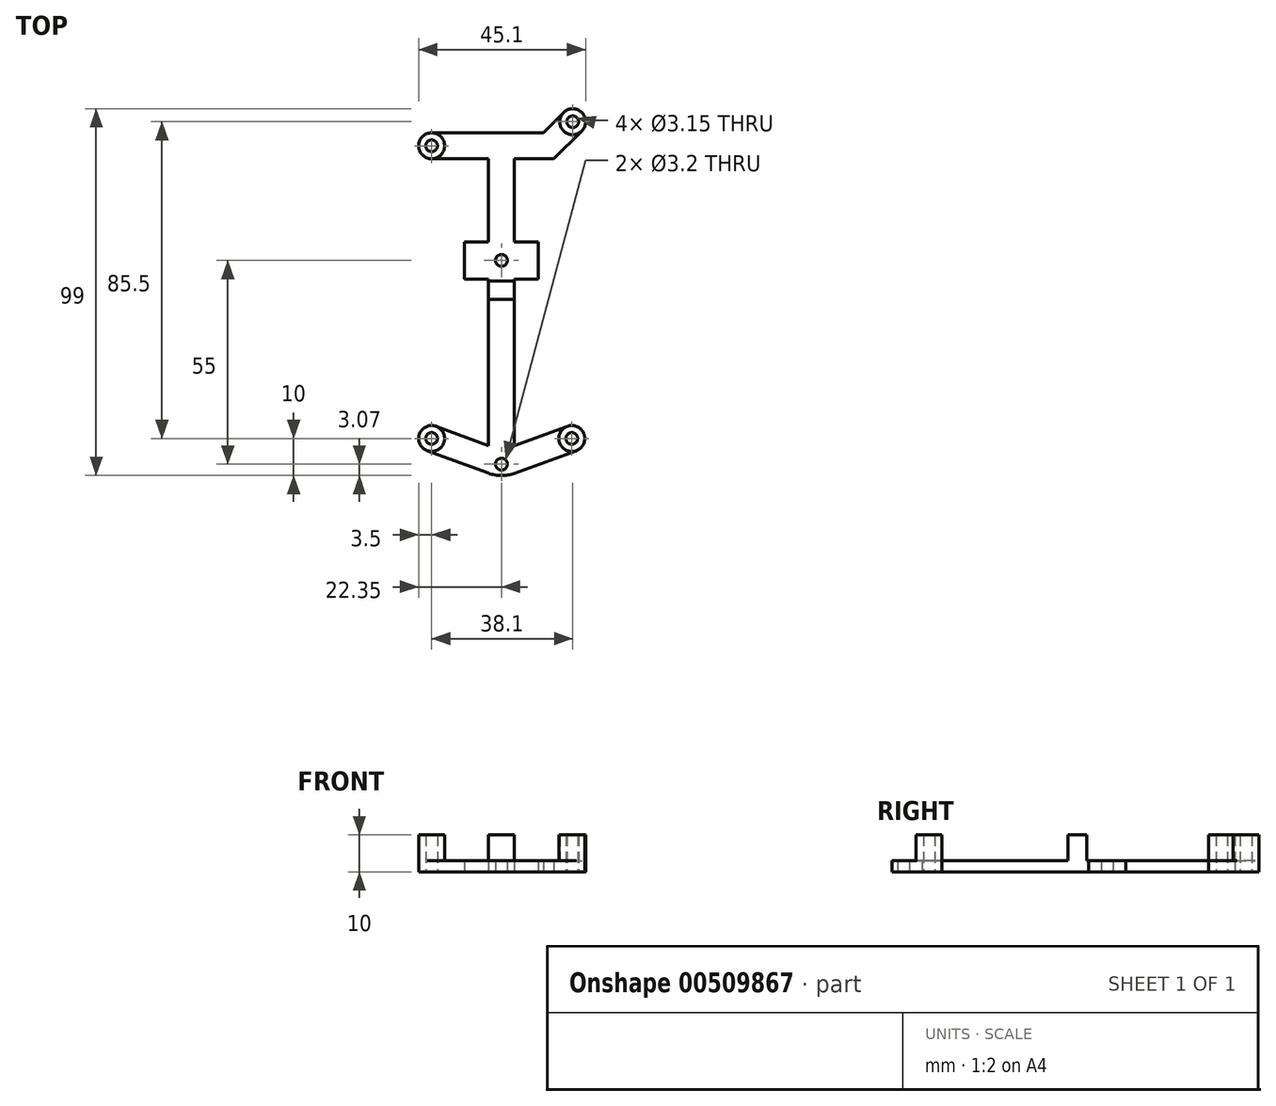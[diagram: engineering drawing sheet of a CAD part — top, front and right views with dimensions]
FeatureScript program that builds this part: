
annotation { "Feature Type Name" : "Feature", "Feature Type Description" : "" }
export const myFeature = defineFeature(function(context is Context, id is Id, definition is map)
    precondition{}
    {
        {
            var Q0;
            Q0=qCreatedBy(makeId("Top.planeOp"),FACE);
            var sketch = newSketch(context, id + "F0", { "sketchPlane" : qUnion([Q0])});
            skCircle(sketch, "E0", {"center": v(6.15, 89) * mm, "radius": 1.6 * mm, "construction": true});
            skCircle(sketch, "E1", {"center": v(44.25, 95.5) * mm, "radius": 1.6 * mm, "construction": true});
            skCircle(sketch, "E2", {"center": v(4.15, 55) * mm, "radius": 1.6 * mm, "construction": true});
            skCircle(sketch, "E3", {"center": v(6.15, 43) * mm, "radius": 1.6 * mm, "construction": true});
            skCircle(sketch, "E4", {"center": v(45.5, 43) * mm, "radius": 1.6 * mm, "construction": true});
            skCircle(sketch, "E5", {"center": v(6.15, 10) * mm, "radius": 1.6 * mm, "construction": true});
            skCircle(sketch, "E6", {"center": v(44, 10) * mm, "radius": 1.6 * mm, "construction": true});
            skLineSegment(sketch, "E7.bottom", {"start": v(0, 0) * mm, "end": v(50, 0) * mm, "construction": true});
            skLineSegment(sketch, "E7.top", {"start": v(0, 100) * mm, "end": v(50, 100) * mm, "construction": true});
            skLineSegment(sketch, "E7.left", {"start": v(0, 0) * mm, "end": v(0, 100) * mm, "construction": true});
            skLineSegment(sketch, "E7.right", {"start": v(50, 0) * mm, "end": v(50, 100) * mm, "construction": true});
            skLineSegment(sketch, "E8", {"start": v(50, 50) * mm, "end": v(0, 50) * mm, "construction": true});
            skSolve(sketch);
        }
        {
            var Q0;
            Q0=qCreatedBy(makeId("Top.planeOp"),FACE);
            var sketch = newSketch(context, id + "F1", { "sketchPlane" : qUnion([Q0])});
            skCircle(sketch, "E9", {"center": v(6.15, 89) * mm, "radius": 1.57 * mm});
            skCircle(sketch, "E10", {"center": v(44.25, 95.5) * mm, "radius": 1.57 * mm});
            skCircle(sketch, "E11", {"center": v(6.15, 10) * mm, "radius": 1.57 * mm});
            skCircle(sketch, "E12", {"center": v(44, 10) * mm, "radius": 1.57 * mm});
            skLineSegment(sketch, "E13", {"start": v(36.3, 92.5) * mm, "end": v(6.15, 92.5) * mm});
            skLineSegment(sketch, "E14", {"start": v(6.15, 85.5) * mm, "end": v(21.49, 85.5) * mm});
            skLineSegment(sketch, "E15", {"start": v(21.49, 8.09) * mm, "end": v(7.36, 13.28) * mm});
            skLineSegment(sketch, "E16", {"start": v(42.8, 13.29) * mm, "end": v(28.49, 8.09) * mm});
            skArc(sketch, "E17", {"start": v(46.72, 93.03) * mm, "mid": v(46.72, 97.97) * mm, "end": v(41.78, 97.97) * mm});
            skArc(sketch, "E18", {"start": v(6.15, 92.5) * mm, "mid": v(2.65, 89) * mm, "end": v(6.15, 85.5) * mm});
            skArc(sketch, "E19", {"start": v(7.36, 13.28) * mm, "mid": v(2.87, 11.2) * mm, "end": v(4.94, 6.72) * mm});
            skArc(sketch, "E20", {"start": v(45.2, 6.71) * mm, "mid": v(47.29, 11.2) * mm, "end": v(42.8, 13.29) * mm});
            skLineSegment(sketch, "E21", {"start": v(36.3, 92.5) * mm, "end": v(41.78, 97.97) * mm});
            skArc(sketch, "E22", {"start": v(21.49, 0.63) * mm, "mid": v(24.99, 0) * mm, "end": v(28.49, 0.62) * mm});
            skLineSegment(sketch, "E23", {"start": v(4.94, 6.72) * mm, "end": v(21.49, 0.63) * mm});
            skLineSegment(sketch, "E24", {"start": v(28.49, 0.62) * mm, "end": v(45.2, 6.71) * mm});
            skLineSegment(sketch, "E25", {"start": v(25, 0) * mm, "end": v(25, 100) * mm, "construction": true});
            skLineSegment(sketch, "E26", {"start": v(21.49, 8.09) * mm, "end": v(19.07, 1.52) * mm, "construction": true});
            skLineSegment(sketch, "E27", {"start": v(21.49, 8.09) * mm, "end": v(28.49, 8.09) * mm, "construction": true});
            skLineSegment(sketch, "E28", {"start": v(44, 10) * mm, "end": v(25, 3.07) * mm, "construction": true});
            skCircle(sketch, "E29", {"center": v(25, 3.07) * mm, "radius": 1.6 * mm});
            skCircle(sketch, "E30", {"center": v(25, 58.07) * mm, "radius": 1.6 * mm});
            skLineSegment(sketch, "E31", {"start": v(21.49, 85.5) * mm, "end": v(21.49, 63.07) * mm});
            skLineSegment(sketch, "E32", {"start": v(21.49, 63.07) * mm, "end": v(15, 63.07) * mm});
            skLineSegment(sketch, "E33", {"start": v(15, 63.07) * mm, "end": v(15, 53.07) * mm});
            skLineSegment(sketch, "E34", {"start": v(15, 53.07) * mm, "end": v(21.49, 53.07) * mm});
            skLineSegment(sketch, "E35", {"start": v(21.49, 53.07) * mm, "end": v(21.49, 8.09) * mm});
            skLineSegment(sketch, "E36", {"start": v(28.49, 8.09) * mm, "end": v(28.49, 53.07) * mm});
            skLineSegment(sketch, "E37", {"start": v(28.49, 53.07) * mm, "end": v(35, 53.07) * mm});
            skLineSegment(sketch, "E38", {"start": v(35, 53.07) * mm, "end": v(35, 63.07) * mm});
            skLineSegment(sketch, "E39", {"start": v(35, 63.07) * mm, "end": v(28.49, 63.07) * mm});
            skLineSegment(sketch, "E40", {"start": v(28.49, 63.07) * mm, "end": v(28.49, 85.5) * mm});
            skLineSegment(sketch, "E41", {"start": v(15, 58.07) * mm, "end": v(35, 58.07) * mm, "construction": true});
            skLineSegment(sketch, "E42", {"start": v(28.49, 85.5) * mm, "end": v(39.2, 85.5) * mm});
            skLineSegment(sketch, "E43", {"start": v(39.2, 85.5) * mm, "end": v(46.72, 93.03) * mm});
            skSolve(sketch);
        }
        {
            var Q0;
            Q0 = qSketchRegion(id + "F1", true);
            extrude(context, id + "F2", {"entities" : qUnion([Q0]), "depth" : 3 * mm});
        }
        {
            var Q0;
            Q0=makeQuery(id+"F2.opExtrude","CAP_FACE",FACE,{"disambiguationData":[OSD([sQuery(id+"F1.wireOp",EDGE,"E9"),sQuery(id+"F1.wireOp",EDGE,"E10"),sQuery(id+"F1.wireOp",EDGE,"E11"),sQuery(id+"F1.wireOp",EDGE,"E12"),sQuery(id+"F1.wireOp",EDGE,"E13"),sQuery(id+"F1.wireOp",EDGE,"E14"),sQuery(id+"F1.wireOp",EDGE,"kDAjYfho-mOMV-DYuy-Qepv-VaYe7mhwmSzW"),sQuery(id+"F1.wireOp",EDGE,"E15"),sQuery(id+"F1.wireOp",EDGE,"gD81GCRO-MMlz-CKZS-rrHH-qSdZNJqOu1tZ"),sQuery(id+"F1.wireOp",EDGE,"E16"),sQuery(id+"F1.wireOp",EDGE,"6TOlm1MV-spuN-TDYP-FoN0-2CfLeE0BN130"),sQuery(id+"F1.wireOp",EDGE,"cyJ5dKEJ-bUzc-47BG-XgNG-o2nG1J2BiiaA"),sQuery(id+"F1.wireOp",EDGE,"E17"),sQuery(id+"F1.wireOp",EDGE,"E18"),sQuery(id+"F1.wireOp",EDGE,"E19"),sQuery(id+"F1.wireOp",EDGE,"E20"),sQuery(id+"F1.wireOp",EDGE,"E21")])],"isStart":false});
            var sketch = newSketch(context, id + "F3", { "sketchPlane" : qUnion([Q0])});
            skCircle(sketch, "E44", {"center": v(6.15, 10) * mm, "radius": 3.5 * mm});
            skCircle(sketch, "E45", {"center": v(6.15, 89) * mm, "radius": 3.5 * mm});
            skCircle(sketch, "E46", {"center": v(44.25, 95.5) * mm, "radius": 3.5 * mm});
            skCircle(sketch, "E47", {"center": v(44, 10) * mm, "radius": 3.5 * mm});
            skLineSegment(sketch, "E48.bottom", {"start": v(21.49, 52.5) * mm, "end": v(28.49, 52.5) * mm});
            skLineSegment(sketch, "E48.top", {"start": v(21.49, 47.5) * mm, "end": v(28.49, 47.5) * mm});
            skLineSegment(sketch, "E48.left", {"start": v(21.49, 52.5) * mm, "end": v(21.49, 47.5) * mm});
            skLineSegment(sketch, "E48.right", {"start": v(28.49, 52.5) * mm, "end": v(28.49, 47.5) * mm});
            skCircle(sketch, "E49", {"center": v(6.15, 10) * mm, "radius": 1.57 * mm});
            skCircle(sketch, "E50", {"center": v(44, 10) * mm, "radius": 1.57 * mm});
            skCircle(sketch, "E51", {"center": v(6.15, 89) * mm, "radius": 1.57 * mm});
            skCircle(sketch, "E52", {"center": v(44.25, 95.5) * mm, "radius": 1.57 * mm});
            skPoint(sketch, "E53", {"position": v(28.49, 50) * mm});
            skSolve(sketch);
        }
        {
            var Q0;
            Q0 = qSketchRegion(id + "F3", true);
            extrude(context, id + "F4", {"entities" : qUnion([Q0]), "operationType" : NewBodyOperationType.ADD, "depth" : 7 * mm});
        }
    });
